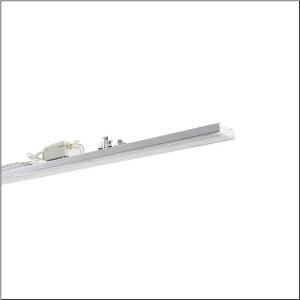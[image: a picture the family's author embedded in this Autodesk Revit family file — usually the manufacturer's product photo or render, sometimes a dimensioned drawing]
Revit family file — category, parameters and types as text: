
# Revit family: licross_r__21_recessed_ho_52tl1edv4l2s_3d33
name_source: partatom
category: Lighting Fixtures
units: mm (PartAtom-declared; Revit-internal decimal feet)

## family parameters
Cut with Voids When Loaded = No
Host = Face
Light Source = No
Part Type = Normal
Room Calculation Point = No
Round Connector Dimension = Use Diameter
Shared = No

## types (1)
- --- (1 x LED, 22130 lm, 125.6 W, 4000K)
    Apparent Load = 126 VA
    CIE Flux Codes = 85 95 99 100 100
    Color Rendering = 80
    Color Temperature = 4000K
    Default Elevation = 1800 mm
    Description = Licross® 21 Recessed HO, luminaire insert, of sheet steel, galvanised, coil coated, white, length: 2.250mm, width: 66mm, height: 67mm, LED rated luminous flux: 22.130lm, light colour: 840, control gear: DALI 2, with plug, 5-pole, with phase selection, mains connection: 220..240V, AC, 50/60Hz, rated input power: 126W, halogen-free wiring, primary light control with lens, of plastic, primary optical cover: cover, of PMMA, light emission: direct distribution, primary light characteristic: symmetric, protection rating (complete): IP40, insulation class (complete): insulation class I (protective earthing), certification: CE, ENEC, VDE, UKCA, protection symbol: D if used in an environment without relevant dust loads with corresponding accessories, impact resistance: IK06, permissible ambient temperature for indoor applications: -40..+30°C, corresponds to IFS (International Featured Standards) requirements for safety and quality in the food industry, reducing of maximum allowable ambient temperature of 5°C with ceiling mounting, LABS conformity tested according to VDMA 24364:2018-05, packaging unit: 1 piece
    Height = 58 mm
    Lamp = 1 x LED
    Lamp Light Flux = 22130 lm
    Lamp Power = 125.6 W
    Lamp count = 1
    Length = 2250 mm
    Luminous efficacy = 176 lm/W
    Manufacturer = Siteco
    ModVariant = No
    Model = 52TL1EDV4L2S
    Mounting Place = Ceiling
    Mounting Type = Pendant
    Number of Poles = 1
    OnlyDefault = Yes
    Power Factor = 1
    Product Name = Licross® 21 Recessed HO
    Product group = luminaire insert
    ProductGroupID = 901
    Protection Class = Protection class I
    Protection Degree = IP 40
    RLX_Detail_Level = 1
    RLX_Emergency_Light_Flux = 0 lm
    RLX_Emergency_Type = 0
    RLX_Emergency_Type_DB = No
    RlxData = <blob elided: 29825 chars, md5=218dad58>
    Socket = socket
    Standby Power = 0 W
    System Light Flux = 22129 lm
    System Power = 126 W
    Type Comments = factory setting: luminous flux: 100 % | dim-lin: 254 | 489 mA
    Type Image = l_1296930.jpg
    URL = http://relux.com
    VarID = @adj_120818
    Voltage = 0 V
    Weight = 0.00 kg
    Width = 66 mm

## geometry (parser evidence)
native form markers: Blend x4, Sweep x12
no freeform markers — native parametric forms only
